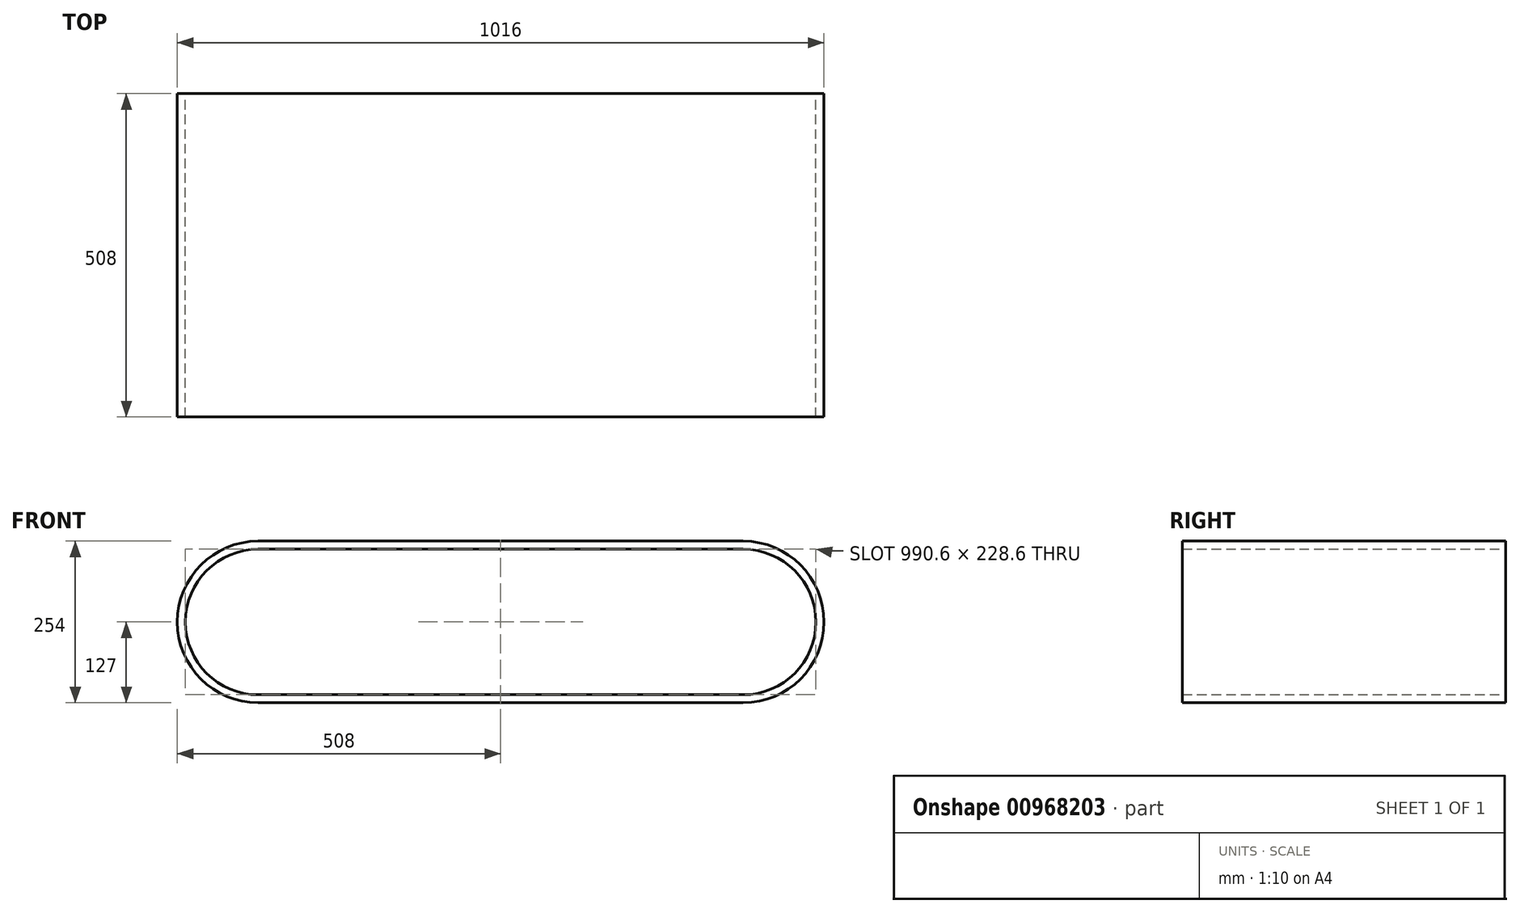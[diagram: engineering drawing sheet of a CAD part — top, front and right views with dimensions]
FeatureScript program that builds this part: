
annotation { "Feature Type Name" : "Feature", "Feature Type Description" : "" }
export const myFeature = defineFeature(function(context is Context, id is Id, definition is map)
    precondition{}
    {
        {
            var Q0;
            Q0=qCreatedBy(makeId("Front.planeOp"),FACE);
            var sketch = newSketch(context, id + "F0", { "sketchPlane" : qUnion([Q0])});
            skCircle(sketch, "E0", {"center": v(0, 0) * mm, "radius": 127 * mm});
            skCircle(sketch, "E1", {"center": v(762, 0) * mm, "radius": 127 * mm});
            skLineSegment(sketch, "E2", {"start": v(0, 127) * mm, "end": v(762, 127) * mm});
            skLineSegment(sketch, "E3", {"start": v(0, -127) * mm, "end": v(762, -127) * mm});
            skSolve(sketch);
        }
        {
            var Q0;
            Q0 = qSketchRegion(id + "F0", true);
            extrude(context, id + "F1", {"entities" : qUnion([Q0]), "depth" : 508 * mm, "offsetDistance" : 25.4 * mm});
        }
        {
            var Q0;
            Q0=makeQuery(id+"F1.opExtrude","CAP_FACE",FACE,{"disambiguationData":[OSD([sQuery(id+"F0.wireOp",EDGE,"E0"),sQuery(id+"F0.wireOp",EDGE,"E1"),sQuery(id+"F0.wireOp",EDGE,"E2"),sQuery(id+"F0.wireOp",EDGE,"E3")])],"isStart":false});
            var Q1;
            Q1=makeQuery(id+"F1.opExtrude","CAP_FACE",FACE,{"disambiguationData":[OSD([sQuery(id+"F0.wireOp",EDGE,"E0"),sQuery(id+"F0.wireOp",EDGE,"E1"),sQuery(id+"F0.wireOp",EDGE,"E2"),sQuery(id+"F0.wireOp",EDGE,"E3")])],"isStart":true});
            shell(context, id + "F2", {"entities" : qUnion([Q0, Q1]), "thickness" : 12.7 * mm});
        }
    });
